# Revit family: IS_iLifeB_T4615_BIM_NL
name_source: partatom
category: Plumbing Fixtures
units: mm (PartAtom-declared; Revit-internal decimal feet)

## family parameters
Always vertical = No
Cut with Voids When Loaded = No
OmniClass Number = 23.45.05.14.27
OmniClass Title = Bidets
Part Type = Normal
Room Calculation Point = No
Round Connector Dimension = Use Diameter
Shared = No
Work Plane-Based = No

## types (4) — shared parameters
Accessories = https://www.idealstandard.nl
Afmetingen = 355 x 540 x 298 mm
AfstandsEenheid = Millimeter
AreaMeasurement = Internal
AreaUnits = millimetres
AssetType = Fixed
Auteur = Ideal Standard
BIMObjectName = IS_IdealStandard_Bidets_i.lifeB_T4615
BIMobject category = Bidets
BIMobject category code = sanitary-bidets
BIMobject main category = Sanitary
BIMobject main category code = sanitary
Beschrijvinggarantie = Herstellergarantie
BidetMounting = wallhung
BimObjectNaam = IS_IdealStandard_Bidets_i.lifeB_T4615
Brand = Ideal Standard
Brand url = https://www.idealstandard.nl
Breedte = 354.349075
Category = Sanitary
Classification = bidets
ConnectionType = Plumbing
CurrencyUnit = €
CurrentRevision = 1
Date of publishing = 22/07/2022
Diepte = 540 mm
DurationUnit = Years
DuurEenheid = Jahre
Edition number = 1
ElementType = Fixed
ExpectedLife = 99
Features = wallhung bidet,  hidden fixation TT0299598, overflow round, in carton box, EU pallet
GarantieduurInstallatie = https://www.idealstandard.nl
Garantieonderdelen = https://www.idealstandard.nl
Garantieunits = Jahre
GemaaktOp = 22/07/2022
Help = https://www.idealstandard.nl
Hoogte = 298.007942199707
Hulp = https://www.idealstandard.nl
IFC Classification = Sanitary Terminal
IfcExportAs = IfcSanitaryTerminalType
IfcExportType = BIDET
Installatieinstructies = https://www.idealstandard.nl
Installation instructions = https://www.idealstandard.nl
InstallationInstructions = https://www.idealstandard.nl
Lengte = 540 mm
LinearUnits = millimetres
MaintenanceInformation = https://www.idealstandard.nl
Manufacturer = Ideal Standard
Manufacturer name = Ideal Standard
ManufacturerURL = https://www.idealstandard.nl
Materiaal = Schamotte
Material = Fireclay
Material main = Fireclay
Merk = Ideal Standard
ModelReference = Ideal Standard i.life B wallhung bidet,  hidden fixation TT0299598, overflow round
NBS Reference Code = 45-35-70/320
NBS Reference Description = Bidets
Name = Bidets_i.lifeB_T4615_IdealStandard
NettWeight = 20.4
Nettogewicht = 20.4
NominalDepth = 540 mm
NominalHeight = 298 mm
NominalLength = 540 mm
NominalWidth = 354 mm
OmniClass Code = 23-31 23 00
OmniClass Description = Bidets
OppervlakteEenheid = Millimeter
PredefinedType = Bidets
Product Guid = a40d1057-ea99-43f3-92f9-6c7145f61f3c
Product SKU = T4615
Product certification = https://www.idealstandard.nl
Product data url = https://bimobject.com
Product family = I.Life B
Product group = Sanitary
Product name = I.Life b wallhung bidet with hidden fixation
Product url = https://www.idealstandard.nl
ProductInformation = https://www.idealstandard.nl
Productinformatie = https://www.idealstandard.nl
QR code = http://bimobject.com
Revisie = 1
Shape = sculptured
Size = 355 x 540 x 298 mm
Space = Internal
SpareParts = https://www.idealstandard.nl
Technical description = https://www.idealstandard.nl
Telefoonnummer = 077 355 08 08
Toepassing = Bidet
Typeconnectie = Installation
UNSPSC Code = 301815
URL = https://www.idealstandard.nl
Uniclass 2015 Code = Pr_40_20_06_11
Uniclass 2015 Name = Bidets
Uniclass2015Beschrijving = Bidets
Uniclass2015Code = Pr_40_20_06_11
Uniclass2015Referentie = Pr_40_20_06_11
Uniclass2015Title = Bidets
Uniclass2015Version = v1.26
Urlproducent = https://www.idealstandard.nl
ValutaEenheid = Euro
Versie = 1
Version = 1
Verwachtelevensduur = 5
VolumeUnits = Liters
Volumeunits = Liter
Vorm = geformt
WRASURL = https://www.wrasapprovals.co.uk
WarrantyDescription = manufacturer warranty
WarrantyDurationUnit = Years
Weight Net (Kg) = 20.4
Wisselstukken = https://www.idealstandard.nl
Youtube clip = https://www.youtube.com
zero-valued in all types: BrutoGewicht, Cost, Default Elevation, Vervangingskosten

## per-type parameters (varying)
| type | Afwerking | Artikelnummer | Artikelomschrijving | Artikelreferentie | BarCode | Barcode | Color | Description | Eigenschappen | Finish | GTIN code | Kleur | MainColor | Model | ModelNumber | Referentie |
| T461501 - Ideal Standard i.life B wallhung bidet,  hidden fixation TT0299598, overflow round - White Finish | Weiss | T461501 | Ideal Standard i.life B Wand-Bidet, verdeckte Befestigung TT0299598, Überlauf rund, weiß, im Karton, EU-Palette | T461501 | 8014140486015 | 8014140486015 | White | Ideal Standard i.life B wallhung bidet,  hidden fixation TT0299598, overflow round, white, in carton box, EU pallet | Wand-Bidet, verdeckte Befestigung TT0299598, Überlauf rund, weiß, im Karton, EU-Palette | White | 8014140486015 | Weiss | White | T461501 | T461501 | IS I.LIFE B Wall Hung WC Bowl Boxed |
| T4615MA - Ideal Standard i.life B wallhung bidet,  hidden fixation TT0299598, overflow round  - Ideal Plus White | Ideal plus Weiß | T4615MA | Ideal Standard i.life B Wand-Bidet, verdeckte Befestigung TT0299598, Überlauf rund, weiß, im Karton, EU-Palette | T4615MA | 8014140486800 | 8014140486800 | Ideal plus White | Ideal Standard i.life B wallhung bidet,  hidden fixation TT0299598, overflow round, white, in carton box, EU pallet | Wand-Bidet, verdeckte Befestigung TT0299598, Überlauf rund, weiß, im Karton, EU-Palette | Ideal plus White | 8014140486800 | Ideal plus Weiß | Ideal plus White | T4615MA | T4615MA | Ideal Standard i.life B wallhung bidet,  hidden fixation TT0299598, overflow round |
| T4615HY - Ideal Standard i.life B wallhung bidet,  hidden fixation TT0299598, overflow round  - Antibacterial glaze Smartguard+ | Weiss Smartguard+ | T4615HY | Ideal Standard i.life B Wand-Bidet, verdeckte Befestigung TT0299598, Überlauf rund, weiß, im Karton, EU-Palette | T4615HY | 8014140514664 | 8014140514664 | White Smartguard+ | Ideal Standard i.life B wallhung bidet,  hidden fixation TT0299598, overflow round, antibacterial glaze Smartguard+, in carton box, EU pallet | wandhängendes Bidet, verdeckte Befestigung TT0299598, Überlauf rund, antibakterielle Glasur Smartguard+, im Karton, EU-Palette | White Smartguard+ | 8014140514664 | Weiss Smartguard+ | White Smartguard+ | T4615HY | T4615HY | Ideal Standard i.life B wallhung bidet,  hidden fixation TT0299598, overflow round |
| T461558 - Ideal Standard i.life B wallhung bidet,  hidden fixation TT0299598, overflow round - Glossy grey | Glänzend grau | T461558 | Ideal Standard i.life B Wand-Bidet, verdeckte Befestigung TT0299598, Überlauf rund, glänzend grau, im Karton, EU-Palette | T461558 | 8014140511649 | 8014140511649 | Glossy grey | Ideal Standard i.life B wallhung bidet,  hidden fixation TT0299598, overflow round, glossy grey, in carton box, EU pallet | Wand-Bidet, verdeckte Befestigung TT0299598, Überlauf rund, weiß, im Karton, EU-Palette | Glossy grey | 8014140511649 | Glänzend grau | Glossy grey | T461558 | T461558 | IS I.LIFE B Wall Hung WC Bowl Boxed |

## geometry (parser evidence)
native form markers: Blend x4, Sweep x3
no freeform markers — native parametric forms only
